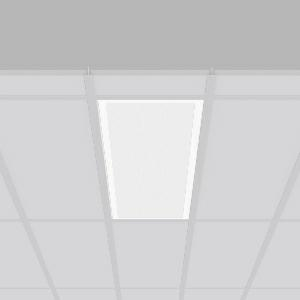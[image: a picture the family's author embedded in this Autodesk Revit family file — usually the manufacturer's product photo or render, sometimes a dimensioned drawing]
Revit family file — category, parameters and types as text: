
# Revit family: sidelite_eco_312368_002_76_d55a
name_source: partatom
category: Lighting Fixtures
units: mm (PartAtom-declared; Revit-internal decimal feet)

## family parameters
Cut with Voids When Loaded = No
Host = Face
Light Source = No
Part Type = Normal
Room Calculation Point = No
Round Connector Dimension = Use Diameter
Shared = No

## types (1)
- MultiLumen 1 (1 x LED Modul 830, 3200 lm, 3000)
    Apparent Load = 29 VA
    CIE Flux Codes = 64 88 97 100 100
    Color Rendering = 80
    Color Temperature = 3000
    Default Elevation = 1800 mm
    Description = Series: SIDELITE ECO
Highly economical recessed luminaire with progressive LED technology. Frame made of aluminium, powder-coated. Diffuser plastic microprismatic. Lightguide and diffuser made of non-yellowing plastic (PMMA). Lateral light emission (RZB SIDELITE technology) for homogeneous light distribution. External driver. External driver with simple plug-in locking system and extended converter connecting cable to luminaire (1.90 m). MultiLumen: 4 steps adjustable luminous flux. Factory setting is the lowest offered step. Luminaire can be used with accessories (to be ordered separately) as recessed or surface mounting luminaire. Perfect for office areas (RUG < 19) and environments with computer screens in accordance with EN 12464-1. Qualified for use in the food and drink industry. 
Colour: white
Length: 1245 mm
Width: 308 mm
Cut-out length: 1233 mm
Cut-out width: 296 mm
Recess height: 160 mm
Luminaire: recess height: 38 mm
Lamp: LED
Socket: without socket
Colour temperature: 3000K
Colour rendering index (CRI): 80
System power: 29 W
Rated luminous flux: 3200 lm
Luminous efficiency: 110 lm/W
System power 2: 33 W
Rated luminous flux 2: 3500 lm
Luminous efficiency 2: 106 lm/W
System power 3: 35 W
Rated luminous flux 3: 3700 lm
Luminous efficiency 3: 106 lm/W
System power 4: 38 W
Rated luminous flux 4: 4000 lm
Luminous efficiency 4: 105 lm/W
Control gear: Converter, dimmable, DALI
Protection class: II
Type of protection: IP 40
    Height = 0 mm  [stored 0 ft]
    Lamp = 1 x LED Modul 830
    Lamp Light Flux = 3200 lm
    Lamp count = 1
    Length = 1245 mm
    Lifetime = 50000 h
    Luminous efficacy = 110 lm/W
    Manufacturer = RZB
    ModVariant = No
    Model = 312368.002.76
    Mounting Place = Ceiling
    Mounting Type = Recessed
    Number of Poles = 1
    OnlyDefault = Yes
    Power Factor = 1
    Product Name = SIDELITE ECO
    Product group = Recessed modular luminaires
    ProductGroupID = 406
    Protection Class = Protection class II
    Protection Degree = IP 20
    RLX_Detail_Level = 1
    RLX_Emergency_Light_Flux = 0 lm
    RLX_Emergency_Type = 0
    RLX_Emergency_Type_DB = No
    RlxData = <blob elided: 35957 chars, md5=31e20685>
    Socket = socket
    Standby Power = 0 W
    System Light Flux = 3200 lm
    System Power = 29 W
    Type Comments = MultiLumen 1
    Type Image = 312368.002.jpg
    URL = http://relux.com
    VarID = multilumen_1
    Voltage = 230 V
    Voltage Range = 220-240 V
    Weight = 0.00 kg
    Width = 308 mm

note: [stored X ft] marks values corroborated as IEEE doubles in the binary element streams (Revit-internal decimal feet)

## geometry (parser evidence)
native form markers: Blend x4, Sweep x9
no freeform markers — native parametric forms only
